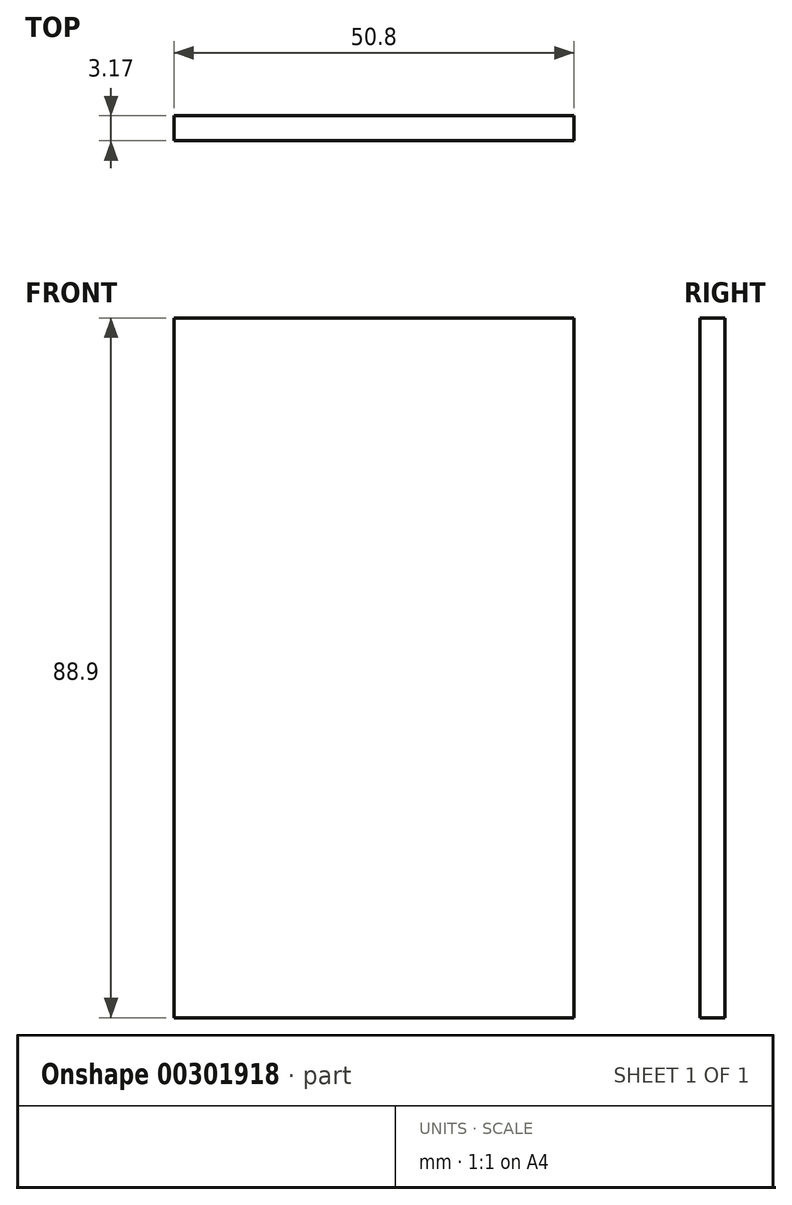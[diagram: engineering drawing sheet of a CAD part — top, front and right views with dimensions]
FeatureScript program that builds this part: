
annotation { "Feature Type Name" : "Feature", "Feature Type Description" : "" }
export const myFeature = defineFeature(function(context is Context, id is Id, definition is map)
    precondition{}
    {
        {
            var Q0;
            Q0=qCreatedBy(makeId("Front.planeOp"),FACE);
            var sketch = newSketch(context, id + "F0", { "sketchPlane" : qUnion([Q0])});
            skLineSegment(sketch, "E0.bottom", {"start": v(25.4, -44.45) * mm, "end": v(-25.4, -44.45) * mm});
            skLineSegment(sketch, "E0.top", {"start": v(25.4, 44.45) * mm, "end": v(-25.4, 44.45) * mm});
            skLineSegment(sketch, "E0.left", {"start": v(25.4, -44.45) * mm, "end": v(25.4, 44.45) * mm});
            skLineSegment(sketch, "E0.right", {"start": v(-25.4, -44.45) * mm, "end": v(-25.4, 44.45) * mm});
            skPoint(sketch, "E0.middle", {"position": v(0, 0) * mm});
            skSolve(sketch);
        }
        {
            var Q0;
            Q0=makeQuery(id+"F0.imprint","IMPRINT",FACE,{"disambiguationData":[TD([[makeQuery(id+"F0.imprint","IMPRINT",EDGE,{"derivedFrom":sQuery(id+"F0.wireOp",EDGE,"E0.bottom")}),-1.0]])]});
            extrude(context, id + "F1", {"entities" : qUnion([Q0]), "depth" : 3.17 * mm});
        }
    });
